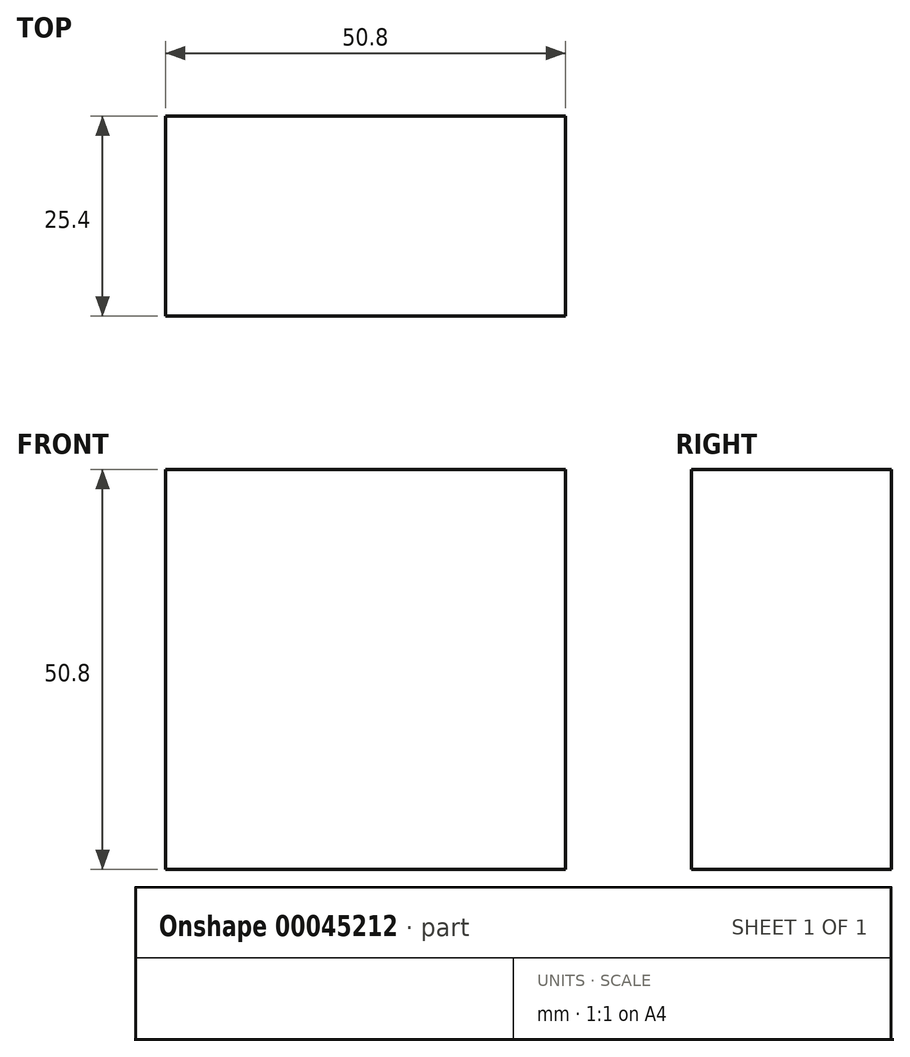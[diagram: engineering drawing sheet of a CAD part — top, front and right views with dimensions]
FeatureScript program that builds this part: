
annotation { "Feature Type Name" : "Feature", "Feature Type Description" : "" }
export const myFeature = defineFeature(function(context is Context, id is Id, definition is map)
    precondition{}
    {
        {
            var Q0;
            Q0=qCreatedBy(makeId("Front.planeOp"),FACE);
            var sketch = newSketch(context, id + "F0", { "sketchPlane" : qUnion([Q0])});
            skLineSegment(sketch, "E0.rect.bottom", {"start": v(25.4, -25.4) * mm, "end": v(-25.4, -25.4) * mm});
            skLineSegment(sketch, "E0.rect.top", {"start": v(25.4, 25.4) * mm, "end": v(-25.4, 25.4) * mm});
            skLineSegment(sketch, "E0.rect.left", {"start": v(25.4, -25.4) * mm, "end": v(25.4, 25.4) * mm});
            skLineSegment(sketch, "E0.rect.right", {"start": v(-25.4, -25.4) * mm, "end": v(-25.4, 25.4) * mm});
            skPoint(sketch, "E0.rect.middle", {"position": v(0, 0) * mm});
            skSolve(sketch);
        }
        {
            var Q0;
            Q0 = qSketchRegion(id + "F0", true);
            extrude(context, id + "F1", {"entities" : qUnion([Q0]), "depth" : 25.4 * mm});
        }
    });
